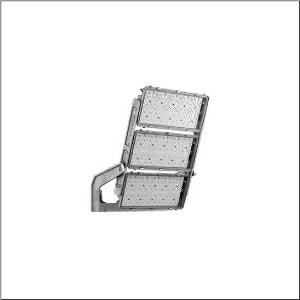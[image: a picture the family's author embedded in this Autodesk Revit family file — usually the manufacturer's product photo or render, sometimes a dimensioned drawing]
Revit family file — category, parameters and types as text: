
# Revit family: floodlight_fl_11_maxi_pro_remote___pl64blc_5xa779427w01aa_301c
name_source: partatom
category: Lighting Fixtures
units: mm (PartAtom-declared; Revit-internal decimal feet)

## family parameters
Cut with Voids When Loaded = No
Host = Face
Light Source = No
Part Type = Normal
Room Calculation Point = No
Round Connector Dimension = Use Diameter
Shared = No

## types (1)
- --- (1 x LED, 142820 lm, 1517.1 W, 5000K)
    Apparent Load = 1517 VA
    CIE Flux Codes = 28 83 99 100 100
    Color Rendering = 70
    Color Temperature = 5000K
    Default Elevation = 1800 mm
    Description = Floodlight FL 11  maxi  pro Remote floodlight; light control with lens of PMMA; cover panel of toughened safety glass, transparent; light distribution: PL64BLC, asymmetric direct distribution, LEDcolour temperature: 5000K, rated luminous flux: 142.820lm, colour rendering: CRI > 70, light colour: 750; luminous efficacy: 94lm/W; brightness control: DALI 2 (1 DALI address); with terminal, 8-pole, max. 2.5mm², mains connection: 220..240V/380..400V AC, 50/60Hz, surge voltage resistance: line to ground: 10kV, ECG replaceable separately, no afterglow with DALI off / DMX off command, LED unit replaceable without ESD environment, dustproof LED module, dimming range 10..100%; 1517W floodlight with 2x LED unit of diecast aluminium, coated grey; length: 713mm / width: 651mm / height: 338mm; mounting bracket, of diecast aluminium, uncoated, natural, equipment: Power, protection rating (complete): IP66; insulation class (complete): insulation class I (protective earthing); certification: CE, ENEC, VDE; ball protection: ball impact resistance with accessories, impact resistance: IK07; only for outdoor installations, rated ambient temperature 10°C, permissible operating ambient temperature: -40..+30°C, permissible storage temperature: -40..+85°Cpackaging unit: 1 piece

Light Distribution: PL64BLC
    Height = 320 mm
    Lamp = 1 x LED
    Lamp Light Flux = 142820 lm
    Lamp Power = 1517.1 W
    Lamp count = 1
    Length = 1002 mm
    Luminous efficacy = 94 lm/W
    Manufacturer = Siteco
    ModVariant = No
    Model = 5XA779427W01AA
    Mounting Place = Ceiling
    Mounting Type = Surface mounted
    Number of Poles = 1
    OnlyDefault = Yes
    Power Factor = 1
    Product Name = Floodlight FL 11 maxi pro Remote | PL64BLC
    Product group = floodlight | ceiling mounted
    ProductGroupID = 301
    Protection Class = Protection class I
    Protection Degree = IP 66
    RLX_Detail_Level = 1
    RLX_Emergency_Light_Flux = 0 lm
    RLX_Emergency_Type = 0
    RLX_Emergency_Type_DB = No
    RlxData = <blob elided: 52201 chars, md5=8f0e1681>
    Socket = socket
    Standby Power = 0 W
    System Light Flux = 142820 lm
    System Power = 1517 W
    Type Comments = factory setting: luminous flux: 100 % | dim-lin: 254 | 1070 mA
    Type Image = l_1349141.jpg
    URL = http://relux.com
    VarID = @adj_080988
    Voltage = 0 V
    Weight = 0.00 kg
    Width = 655 mm

## geometry (parser evidence)
native form markers: Blend x4, Sweep x14
no freeform markers — native parametric forms only
